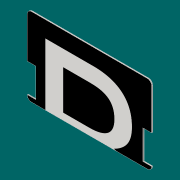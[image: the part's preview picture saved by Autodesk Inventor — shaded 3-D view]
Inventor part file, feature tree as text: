
AUTODESK INVENTOR PART (.ipt)
format: ipt  version: 2016 (Build 200138000, 138)  size: 207,360 bytes
history: native  units: mm
features: sketch x5, other x4, extrude x3, projected_geometry x3, fillet x1, mirror x1
ambient origin geometry x8: Origin, YZ Plane, XZ Plane, XY Plane, X Axis, Y Axis, Z Axis, Center Point
bodies: Solid1 (feature_tree)
feature tree (17):
  extrude  "Extrusion1"  Depth=53.98mm
  fillet  "Fillet1"  Radius=0.76mm
  extrude  "Extrusion2"  Depth=2.88mm
  extrude  "Extrusion3"  Depth=5.588mm
  mirror  "Mirror1"
  other  "Decal1"
  other  "Decal2"
  sketch  "Sketch1"  dims[d0=85.6mm d1=53.98mm d2=0.76mm]
  sketch  "Sketch2"  dims[d3=0.0mm d4=2.88mm]
  projected_geometry  "Projected Loop1"
  sketch  "Sketch3"  dims[d5=5.588mm d6=5.588mm]
  sketch  "Sketch4"  dims[d7=3.0mm]
  projected_geometry  "Projected Loop2"
  sketch  "Sketch5"  dims[d8=3.0mm d9=20.0mm d10=20.0mm d11=0.76mm d12=0.0mm d13=3.0mm d14=3.0mm d15=0.76mm d16=1.5mm d17=1.5mm d18=1.5mm d19=0.76mm d20=0.0mm]
  projected_geometry  "Projected Loop3"
  other  "Image4"
  other  "Image5"
